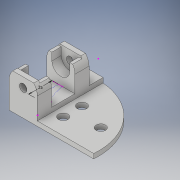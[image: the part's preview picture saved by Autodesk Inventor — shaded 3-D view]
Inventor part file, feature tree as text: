
AUTODESK INVENTOR PART (.ipt)
format: ipt  version: 2018 (Build 220112000, 112)  size: 218,112 bytes
history: native  units: in
note: dims shown in document units (in); Inventor stores cm internally (conversion verified against a paired STEP export)
features: plane x9, extrude x7, sketch x7, mirror x1
ambient origin geometry x8: Origin, YZ Plane, XZ Plane, XY Plane, X Axis, Y Axis, Z Axis, Center Point
bodies: Solid1 (feature_tree)
feature tree (24):
  plane  "Work Plane12"
  extrude  "Extrusion2"  Depth=1.1811in
  plane  "Work Plane7"
  plane  "Work Plane6"
  sketch  "Sketch7"  dims[d14=0.7874in d15=1.378in]
  plane  "Work Plane8"
  extrude  "Extrusion7"  Depth=1.378in
  plane  "Work Plane9"
  extrude  "Extrusion8"  Depth=0.748in
  plane  "Work Plane10"
  extrude  "Extrusion9"  Depth=0.1969in TaperAngle=0.0deg
  plane  "Work Plane2"
  mirror  "Mirror2"
  plane  "Work Plane11"
  extrude  "Extrusion10"  Depth=0.9843in TaperAngle=0.0deg
  plane  "Work Plane14"
  extrude  "Extrusion16"  Depth=0.1969in TaperAngle=0.0deg
  extrude  "Extrusion17"  TaperAngle=90.0deg  [1 undecoded]
  sketch  "Sketch2"  dims[d9=0.1969in d10=0.0in d13=1.1811in]
  sketch  "Sketch8"  dims[d45=0.5906in d46=0.0in d47=0.748in]
  sketch  "Sketch10"  dims[d48=0.3937in d49=0.0in d51=0.1969in d52=0.0in]
  sketch  "Sketch11"  dims[d54=0.9843in d55=3.1496in d56=0.0in]
  sketch  "Sketch17"  dims[d94=3.5433in d95=0.1969in d96=0.0in]
  sketch  "Sketch18"  dims[d98=2.7559in d99=90.0deg d100=1.1811in d101=1.1811in d102=0.3937in d103=0.315in d104=1.5748in d105=0.3937in d106=0.7874in d107=0.7874in d108=0.3937in d109=0.3937in d110=0.3937in d111=0.1969in d112=0.0in]
note: 1 required parameter value undecoded (feature->parameter linkage not recoverable at this tier; creation-order binding heuristic only, values carry confidence <= 0.55)
